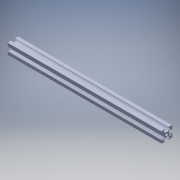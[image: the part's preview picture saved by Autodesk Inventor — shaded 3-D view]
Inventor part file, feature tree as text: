
AUTODESK INVENTOR PART (.ipt)
format: ipt  version: 2018 (Build 220112000, 112)  size: 354,816 bytes
history: native  units: in
note: dims shown in document units (in); Inventor stores cm internally (conversion verified against a paired STEP export)
features: extrude x1, sketch x1, projected_geometry x1, fillet x1
ambient origin geometry x8: Origin, YZ Plane, XZ Plane, XY Plane, X Axis, Y Axis, Z Axis, Center Point
bodies: Solid1 (feature_tree)
feature tree (4):
  extrude  "Extrusion2"  [1 undecoded]
  sketch  "Sketch3"  dims[d2=7.4803in d3=0.0in]
  projected_geometry  "Projected Loop2"
  fillet  "Fillet5"  [1 undecoded]
note: 2 required parameter values undecoded (feature->parameter linkage not recoverable at this tier; creation-order binding heuristic only, values carry confidence <= 0.55)
